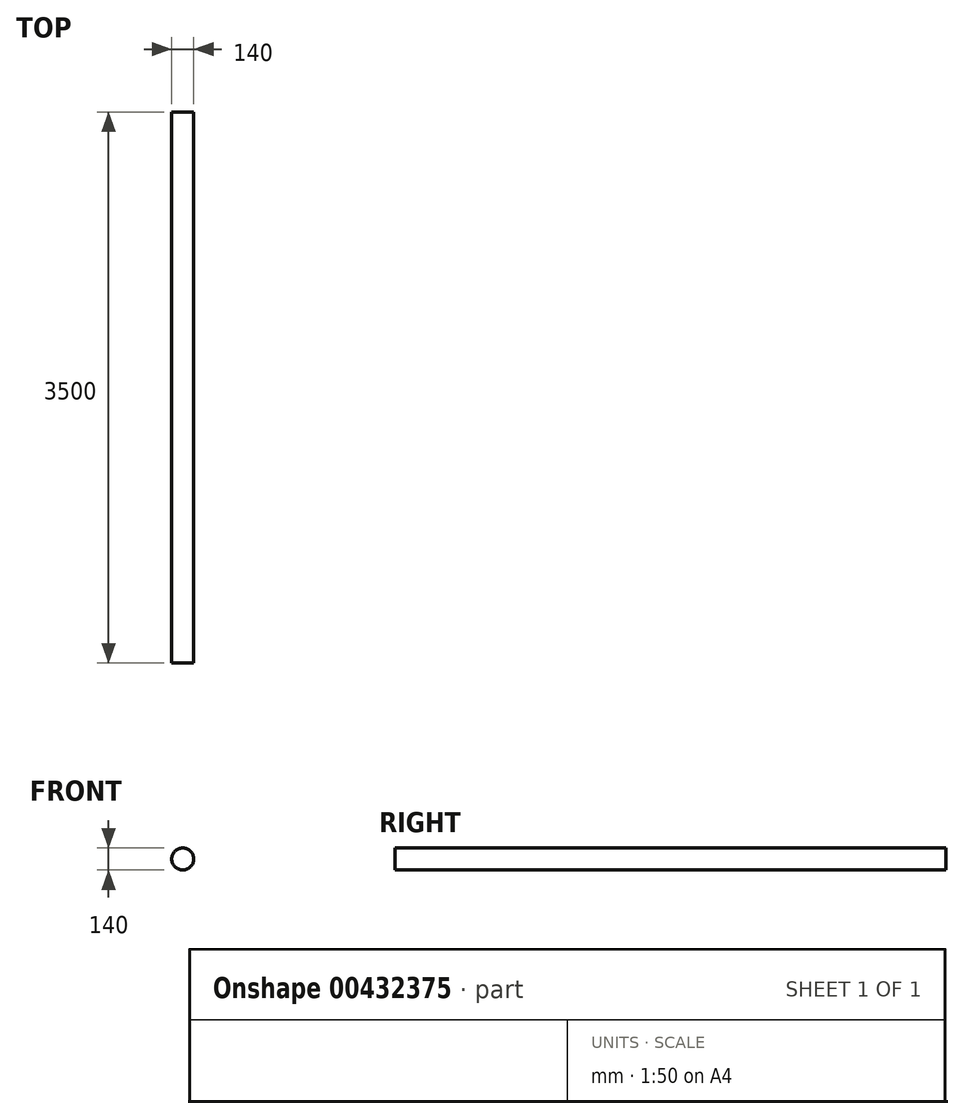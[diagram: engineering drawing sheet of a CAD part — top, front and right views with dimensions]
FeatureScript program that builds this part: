
annotation { "Feature Type Name" : "Feature", "Feature Type Description" : "" }
export const myFeature = defineFeature(function(context is Context, id is Id, definition is map)
    precondition{}
    {
        {
            var Q0;
            Q0=qCreatedBy(makeId("Front.planeOp"),FACE);
            var sketch = newSketch(context, id + "F0", { "sketchPlane" : qUnion([Q0])});
            skCircle(sketch, "E0", {"center": v(0, 0) * mm, "radius": 70 * mm});
            skSolve(sketch);
        }
        {
            var Q0;
            Q0=makeQuery(id+"F0.imprint","IMPRINT",FACE,{"disambiguationData":[TD([[makeQuery(id+"F0.imprint","IMPRINT",EDGE,{"derivedFrom":sQuery(id+"F0.wireOp",EDGE,"E0")}),1.0]])]});
            extrude(context, id + "F1", {"entities" : qUnion([Q0]), "depth" : 3500 * mm});
        }
    });
